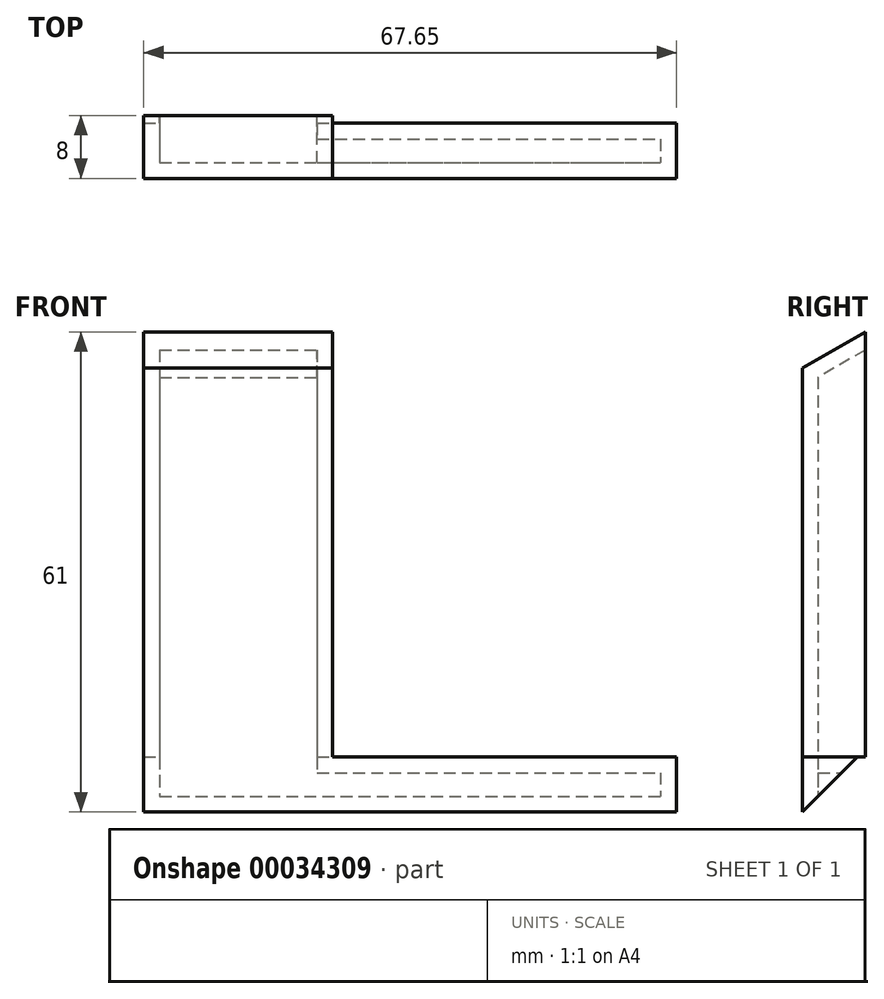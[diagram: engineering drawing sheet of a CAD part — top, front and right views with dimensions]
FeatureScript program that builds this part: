
annotation { "Feature Type Name" : "Feature", "Feature Type Description" : "" }
export const myFeature = defineFeature(function(context is Context, id is Id, definition is map)
    precondition{}
    {
        {
            var Q0;
            Q0=qCreatedBy(makeId("Front.planeOp"),FACE);
            var sketch = newSketch(context, id + "F0", { "sketchPlane" : qUnion([Q0])});
            skLineSegment(sketch, "E0.rect.bottom", {"start": v(-12, 27) * mm, "end": v(12, 27) * mm, "construction": true});
            skLineSegment(sketch, "E0.rect.top", {"start": v(-12, -27) * mm, "end": v(12, -27) * mm, "construction": true});
            skLineSegment(sketch, "E0.rect.left", {"start": v(-12, 27) * mm, "end": v(-12, -27) * mm, "construction": true});
            skLineSegment(sketch, "E0.rect.right", {"start": v(12, 27) * mm, "end": v(12, -27) * mm, "construction": true});
            skPoint(sketch, "E0.rect.middle", {"position": v(0, 0) * mm});
            skLineSegment(sketch, "E1.rect.bottom", {"start": v(-12, 27) * mm, "end": v(12, 27) * mm});
            skLineSegment(sketch, "E1.rect.top", {"start": v(-12, -27) * mm, "end": v(12, -27) * mm});
            skLineSegment(sketch, "E1.rect.left", {"start": v(-12, 27) * mm, "end": v(-12, -27) * mm});
            skLineSegment(sketch, "E1.rect.right", {"start": v(12, 27) * mm, "end": v(12, -27) * mm});
            skLineSegment(sketch, "E2.rect.bottom", {"start": v(-10, 25) * mm, "end": v(10, 25) * mm});
            skLineSegment(sketch, "E2.rect.top", {"start": v(-10, -25) * mm, "end": v(10, -25) * mm});
            skLineSegment(sketch, "E2.rect.left", {"start": v(-10, 25) * mm, "end": v(-10, -25) * mm});
            skLineSegment(sketch, "E2.rect.right", {"start": v(10, 25) * mm, "end": v(10, -25) * mm});
            skLineSegment(sketch, "E3", {"start": v(-10, -25) * mm, "end": v(-10, -27) * mm});
            skLineSegment(sketch, "E4", {"start": v(10, -25) * mm, "end": v(10, -27) * mm});
            skSolve(sketch);
        }
        {
            var Q0;
            Q0=makeQuery(id+"F0.imprint","IMPRINT",FACE,{"disambiguationData":[TD([[makeQuery(id+"F0.imprint","IMPRINT",EDGE,{"derivedFrom":sQuery(id+"F0.wireOp",EDGE,"E1.rect.bottom")}),-1.0]])]});
            var Q1;
            Q1=makeQuery(id+"F0.imprint","IMPRINT",FACE,{"disambiguationData":[TD([[makeQuery(id+"F0.imprint","IMPRINT",EDGE,{"derivedFrom":sQuery(id+"F0.wireOp",EDGE,"E2.rect.bottom")}),-1.0]])]});
            var Q2;
            Q2=makeQuery(id+"F0.imprint","IMPRINT",FACE,{"disambiguationData":[TD([[makeQuery(id+"F0.imprint","IMPRINT",EDGE,{"derivedFrom":sQuery(id+"F0.wireOp",EDGE,"E2.rect.top")}),-1.0]])]});
            extrude(context, id + "F1", {"entities" : qUnion([Q0, Q1, Q2]), "depth" : 8 * mm});
        }
        {
            var Q0;
            Q0=qCreatedBy(makeId("Right.planeOp"),FACE);
            var sketch = newSketch(context, id + "F2", { "sketchPlane" : qUnion([Q0])});
            skLineSegment(sketch, "E5", {"start": v(0, -22.38) * mm, "end": v(-8, -27) * mm});
            skLineSegment(sketch, "E6", {"start": v(0, -22.38) * mm, "end": v(0, -27) * mm});
            skLineSegment(sketch, "E7", {"start": v(0, -27) * mm, "end": v(-8, -27) * mm});
            skLineSegment(sketch, "E8", {"start": v(0, 27) * mm, "end": v(-8, 22.38) * mm});
            skLineSegment(sketch, "E9", {"start": v(-8, 22.38) * mm, "end": v(-8, 27) * mm});
            skLineSegment(sketch, "E10", {"start": v(-8, 27) * mm, "end": v(0, 27) * mm});
            skLineSegment(sketch, "E11", {"start": v(-6.5, -26.13) * mm, "end": v(-8, -26.13) * mm, "construction": true});
            skLineSegment(sketch, "E12", {"start": v(-6.5, -24.13) * mm, "end": v(-1.5, -21.25) * mm});
            skLineSegment(sketch, "E13", {"start": v(-6.5, 21.25) * mm, "end": v(-1.5, 24.13) * mm});
            skLineSegment(sketch, "E14", {"start": v(-6.5, -24.13) * mm, "end": v(-6.5, 21.25) * mm});
            skLineSegment(sketch, "E15", {"start": v(-1.5, 24.13) * mm, "end": v(-1.5, -21.25) * mm});
            skLineSegment(sketch, "E16", {"start": v(-6.5, -24.13) * mm, "end": v(-6.5, -26.13) * mm});
            skLineSegment(sketch, "E17", {"start": v(-1.5, -21.25) * mm, "end": v(-1.5, -23.25) * mm});
            skLineSegment(sketch, "E18", {"start": v(-6.5, 21.25) * mm, "end": v(-6.5, 23.25) * mm});
            skLineSegment(sketch, "E19", {"start": v(-1.5, 24.13) * mm, "end": v(-1.5, 26.13) * mm});
            skLineSegment(sketch, "E20", {"start": v(-8, 22.38) * mm, "end": v(-6.5, 22.38) * mm});
            skLineSegment(sketch, "E21", {"start": v(-1.5, 26.13) * mm, "end": v(0, 26.13) * mm});
            skLineSegment(sketch, "E22", {"start": v(0, -22.38) * mm, "end": v(-1.5, -22.38) * mm, "construction": true});
            skLineSegment(sketch, "E23", {"start": v(-1.5, 24.13) * mm, "end": v(0, 25) * mm});
            skLineSegment(sketch, "E24", {"start": v(0, 25) * mm, "end": v(0.8, 25.47) * mm});
            skLineSegment(sketch, "E25", {"start": v(0, -22.38) * mm, "end": v(0.8, -21.91) * mm});
            skLineSegment(sketch, "E26", {"start": v(0.8, -21.91) * mm, "end": v(0.8, 25.47) * mm});
            skLineSegment(sketch, "E27", {"start": v(-1.5, -21.25) * mm, "end": v(0.8, -19.91) * mm});
            skLineSegment(sketch, "E28", {"start": v(-6.5, -24.13) * mm, "end": v(-8.13, -25.08) * mm});
            skLineSegment(sketch, "E29", {"start": v(-8.13, -25.08) * mm, "end": v(-8, -27) * mm});
            skLineSegment(sketch, "E30", {"start": v(0.8, -20.24) * mm, "end": v(-8.1, -25.39) * mm});
            skSolve(sketch);
        }
        {
            var Q0;
            {var subQ1=sQuery(id+"F2.wireOp",EDGE,"E9");Q0=makeQuery(id+"F2.imprint","IMPRINT",FACE,{"disambiguationData":[TD([[makeQuery(id+"F2.imprint","IMPRINT",EDGE,{"derivedFrom":subQ1}),-1.0]])]});}
            extrude(context, id + "F3", {"entities" : qUnion([Q0]), "operationType" : NewBodyOperationType.REMOVE, "oppositeDirection" : true, "depth" : 50 * mm});
        }
        {
            var Q0;
            {var subQ1=sQuery(id+"F2.wireOp",EDGE,"E9");Q0=makeQuery(id+"F2.imprint","IMPRINT",FACE,{"disambiguationData":[TD([[makeQuery(id+"F2.imprint","IMPRINT",EDGE,{"derivedFrom":subQ1}),-1.0]])]});}
            extrude(context, id + "F4", {"entities" : qUnion([Q0]), "operationType" : NewBodyOperationType.REMOVE, "depth" : 25.4 * mm});
        }
        {
            var Q0;
            Q0=makeQuery(id+"F1.opExtrude","CAP_FACE",FACE,{"disambiguationData":[OSD([sQuery(id+"F0.wireOp",EDGE,"E1.rect.bottom"),sQuery(id+"F0.wireOp",EDGE,"E1.rect.top"),sQuery(id+"F0.wireOp",EDGE,"E1.rect.left"),sQuery(id+"F0.wireOp",EDGE,"E1.rect.right")])],"isStart":true});
            var Q1;
            Q1=makeQuery(id+"F1.opExtrude","SWEPT_FACE",FACE,{"disambiguationData":[OSD([sQuery(id+"F0.wireOp",EDGE,"E1.rect.top")])]});
            shell(context, id + "F5", {"entities" : qUnion([Q0, Q1]), "thickness" : 2 * mm});
        }
        {
            var Q0;
            Q0=makeQuery(id+"F1.opExtrude","CAP_FACE",FACE,{"disambiguationData":[OSD([sQuery(id+"F0.wireOp",EDGE,"E1.rect.bottom"),sQuery(id+"F0.wireOp",EDGE,"E1.rect.top"),sQuery(id+"F0.wireOp",EDGE,"E1.rect.left"),sQuery(id+"F0.wireOp",EDGE,"E1.rect.right")])],"isStart":true});
            var sketch = newSketch(context, id + "F6", { "sketchPlane" : qUnion([Q0])});
            skLineSegment(sketch, "E31", {"start": v(12, -27) * mm, "end": v(12, -34) * mm});
            skLineSegment(sketch, "E32", {"start": v(12, -34) * mm, "end": v(-55.65, -34) * mm});
            skLineSegment(sketch, "E33", {"start": v(-12, -27) * mm, "end": v(-55.65, -27) * mm});
            skLineSegment(sketch, "E34", {"start": v(10, -27) * mm, "end": v(10, -34) * mm});
            skLineSegment(sketch, "E35", {"start": v(-55.65, -34) * mm, "end": v(-55.65, -27) * mm});
            skLineSegment(sketch, "E36", {"start": v(12, -32) * mm, "end": v(-55.65, -32) * mm});
            skLineSegment(sketch, "E37", {"start": v(-12, -27) * mm, "end": v(-10, -27) * mm});
            skLineSegment(sketch, "E38", {"start": v(-10, -27) * mm, "end": v(10, -27) * mm});
            skLineSegment(sketch, "E39", {"start": v(-10, -27) * mm, "end": v(-10, -29) * mm});
            skLineSegment(sketch, "E40", {"start": v(-10, -29) * mm, "end": v(-55.65, -29) * mm});
            skLineSegment(sketch, "E41", {"start": v(-53.65, -27) * mm, "end": v(-53.65, -34) * mm});
            skLineSegment(sketch, "E42", {"start": v(-10, -32) * mm, "end": v(-10, -34) * mm});
            skLineSegment(sketch, "E43", {"start": v(-10, -28) * mm, "end": v(-55.65, -28) * mm});
            skSolve(sketch);
        }
        {
            var Q0;
            {var subQ0=makeQuery(id+"F1.opExtrude","CAP_EDGE",EDGE,{"disambiguationData":[OSD([sQuery(id+"F0.wireOp",EDGE,"E1.rect.top")])],"isStart":true});Q0=makeQuery(id+"F6.imprint","IMPRINT",FACE,{"disambiguationData":[TD([[makeQuery(id+"F6.imprint","IMPRINT",EDGE,{"derivedFrom":subQ0}),1.0]])]});}
            var Q1;
            {var subQ3=sQuery(id+"F6.wireOp",EDGE,"E31");var subQ5=sQuery(id+"F6.wireOp",EDGE,"E32");var subQ7=makeQuery(id+"F6.imprint","INTERSECT",VERTEX,{"derivedFrom":[subQ3,subQ5]});Q1=makeQuery(id+"F6.imprint","IMPRINT",FACE,{"disambiguationData":[TD([[makeQuery(id+"F6.imprint","IMPRINT",EDGE,{"disambiguationData":[TD([[subQ7,1.0]])],"derivedFrom":subQ3}),-1.0]])]});}
            var Q2;
            {var subQ0=sQuery(id+"F6.wireOp",EDGE,"E42");Q2=makeQuery(id+"F6.imprint","IMPRINT",FACE,{"disambiguationData":[TD([[makeQuery(id+"F6.imprint","IMPRINT",EDGE,{"derivedFrom":subQ0}),1.0]])]});}
            var Q3;
            {var subQ0=sQuery(id+"F6.wireOp",EDGE,"E42");Q3=makeQuery(id+"F6.imprint","IMPRINT",FACE,{"disambiguationData":[TD([[makeQuery(id+"F6.imprint","IMPRINT",EDGE,{"derivedFrom":subQ0}),-1.0]])]});}
            var Q4;
            {var subQ6=sQuery(id+"F6.wireOp",EDGE,"E37");Q4=makeQuery(id+"F6.imprint","IMPRINT",FACE,{"disambiguationData":[TD([[makeQuery(id+"F6.imprint","IMPRINT",EDGE,{"derivedFrom":subQ6}),1.0]])]});}
            var Q5;
            {var subQ3=sQuery(id+"F6.wireOp",EDGE,"E33");var subQ5=sQuery(id+"F6.wireOp",EDGE,"E35");var subQ7=makeQuery(id+"F6.imprint","INTERSECT",VERTEX,{"derivedFrom":[subQ3,subQ5]});Q5=makeQuery(id+"F6.imprint","IMPRINT",FACE,{"disambiguationData":[TD([[makeQuery(id+"F6.imprint","IMPRINT",EDGE,{"disambiguationData":[TD([[subQ7,1.0]])],"derivedFrom":subQ3}),1.0]])]});}
            var Q6;
            {var subQ3=sQuery(id+"F6.wireOp",EDGE,"E35");var subQ5=sQuery(id+"F6.wireOp",EDGE,"E36");var subQ7=makeQuery(id+"F6.imprint","INTERSECT",VERTEX,{"derivedFrom":[subQ3,subQ5]});Q6=makeQuery(id+"F6.imprint","IMPRINT",FACE,{"disambiguationData":[TD([[makeQuery(id+"F6.imprint","IMPRINT",EDGE,{"disambiguationData":[TD([[subQ7,-1.0]])],"derivedFrom":subQ3}),-1.0]])]});}
            var Q7;
            {var subQ3=sQuery(id+"F6.wireOp",EDGE,"E32");var subQ5=sQuery(id+"F6.wireOp",EDGE,"E35");var subQ7=makeQuery(id+"F6.imprint","INTERSECT",VERTEX,{"derivedFrom":[subQ3,subQ5]});Q7=makeQuery(id+"F6.imprint","IMPRINT",FACE,{"disambiguationData":[TD([[makeQuery(id+"F6.imprint","IMPRINT",EDGE,{"disambiguationData":[TD([[subQ7,1.0]])],"derivedFrom":subQ3}),-1.0]])]});}
            var Q8;
            {var subQ6=sQuery(id+"F6.wireOp",EDGE,"E38");Q8=makeQuery(id+"F6.imprint","IMPRINT",FACE,{"disambiguationData":[TD([[makeQuery(id+"F6.imprint","IMPRINT",EDGE,{"derivedFrom":subQ6}),-1.0]])]});}
            var Q9;
            {var subQ3=sQuery(id+"F6.wireOp",EDGE,"E39");var subQ5=sQuery(id+"F6.wireOp",EDGE,"E40");var subQ7=makeQuery(id+"F6.imprint","INTERSECT",VERTEX,{"derivedFrom":[subQ3,subQ5]});Q9=makeQuery(id+"F6.imprint","IMPRINT",FACE,{"disambiguationData":[TD([[makeQuery(id+"F6.imprint","IMPRINT",EDGE,{"disambiguationData":[TD([[subQ7,1.0]])],"derivedFrom":subQ3}),-1.0]])]});}
            var Q10;
            {var subQ3=sQuery(id+"F6.wireOp",EDGE,"E35");var subQ5=sQuery(id+"F6.wireOp",EDGE,"E40");var subQ7=makeQuery(id+"F6.imprint","INTERSECT",VERTEX,{"derivedFrom":[subQ3,subQ5]});Q10=makeQuery(id+"F6.imprint","IMPRINT",FACE,{"disambiguationData":[TD([[makeQuery(id+"F6.imprint","IMPRINT",EDGE,{"disambiguationData":[TD([[subQ7,-1.0]])],"derivedFrom":subQ3}),-1.0]])]});}
            extrude(context, id + "F7", {"entities" : qUnion([Q0, Q1, Q2, Q3, Q4, Q5, Q6, Q7, Q8, Q9, Q10]), "operationType" : NewBodyOperationType.ADD, "oppositeDirection" : true, "depth" : 8 * mm});
        }
        {
            var Q0;
            Q0=makeQuery(id+"F7.opExtrude","SWEPT_FACE",FACE,{"disambiguationData":[OSD([sQuery(id+"F6.wireOp",EDGE,"E35")])]});
            var sketch = newSketch(context, id + "F8", { "sketchPlane" : qUnion([Q0])});
            skLineSegment(sketch, "E44", {"start": v(-8, -34) * mm, "end": v(0, -26) * mm});
            skSolve(sketch);
        }
        {
            var Q0;
            {var subQ2=sQuery(id+"F8.wireOp",EDGE,"E44");Q0=makeQuery(id+"F8.imprint","IMPRINT",FACE,{"disambiguationData":[TD([[makeQuery(id+"F8.imprint","IMPRINT",EDGE,{"derivedFrom":subQ2}),-1.0]])]});}
            extrude(context, id + "F9", {"entities" : qUnion([Q0]), "operationType" : NewBodyOperationType.REMOVE, "oppositeDirection" : true, "depth" : 76.2 * mm});
        }
        {
            var Q0;
            {var subQ9=sQuery(id+"F6.wireOp",EDGE,"E38");Q0=makeQuery(id+"F6.imprint","IMPRINT",FACE,{"disambiguationData":[TD([[makeQuery(id+"F6.imprint","IMPRINT",EDGE,{"derivedFrom":subQ9}),-1.0]])]});}
            extrude(context, id + "F10", {"entities" : qUnion([Q0]), "operationType" : NewBodyOperationType.REMOVE, "oppositeDirection" : true, "depth" : 6 * mm});
        }
    });
